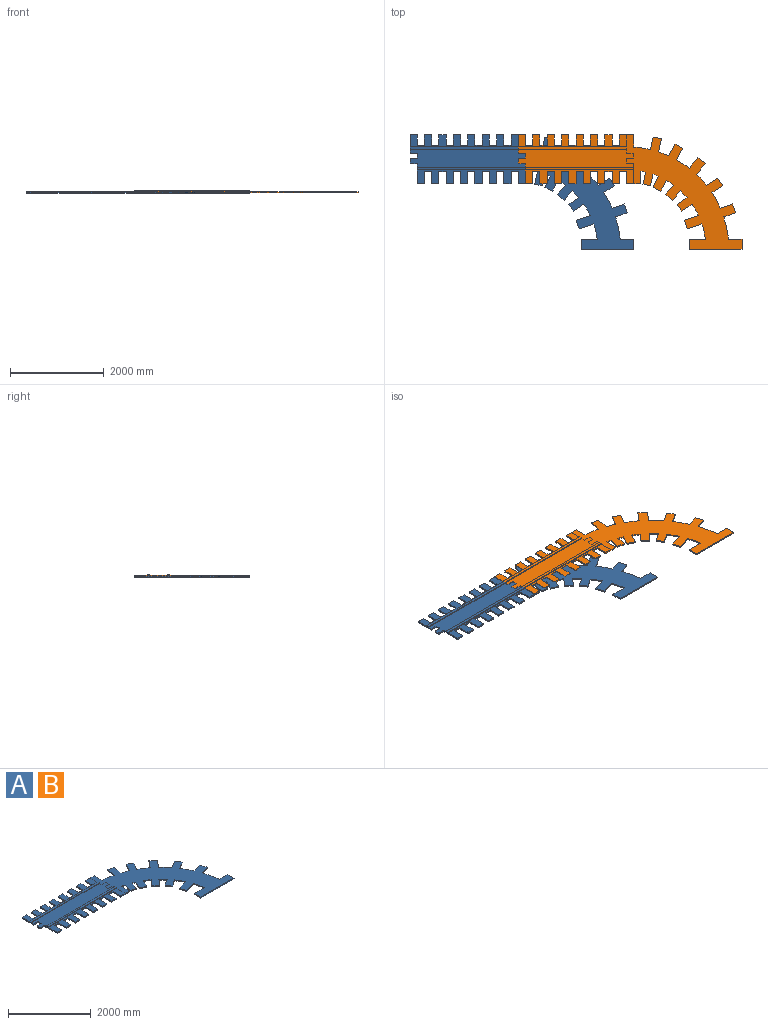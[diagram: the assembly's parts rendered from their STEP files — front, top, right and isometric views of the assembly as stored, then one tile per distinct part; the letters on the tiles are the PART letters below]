
ASSEMBLY  parts=2 mates=1
PART A: 155 faces, bbox 4783.5x2449.5x50.8 mm
  f0: plane 427.85x31.75mm, normal (1,0,0), area 2730.3mm2, adj f4,f67,f68,f86,f97,f137
  f1: plane 294.58x31.75mm, normal (-1,0,0), area 9353.1mm2, adj f4,f39,f86,f95
  f2: plane 81.11x31.75mm, normal (-1,0,0), area 2575.3mm2, adj f4,f29,f86,f88
  f3: plane 81.11x31.75mm, normal (1,0,0), area 2575.3mm2, adj f4,f76,f86,f88,f98
  f4: plane 2468.9x728.98mm, normal (0,0,1), area 1276293.4mm2, adj f0,f1,f2,f3,f29,f30,f31,f32
  f5: plane 154.31x31.75mm, normal (0,1,0), area 4899.2mm2, adj f6,f84,f85,f86
  f6: plane 228.83x31.75mm, normal (1,0,0), area 7265.3mm2, adj f5,f7,f85,f86
  f7: plane 154.31x31.75mm, normal (0,1,0), area 4899.2mm2, adj f6,f8,f85,f86
  f8: plane 228.83x31.75mm, normal (-1,0,0), area 7265.3mm2, adj f7,f9,f85,f86
  f9: plane 154.31x31.75mm, normal (0,1,0), area 4899.2mm2, adj f8,f10,f85,f86
  f10: plane 228.83x31.75mm, normal (1,0,0), area 7265.3mm2, adj f9,f11,f85,f86
  f11: plane 154.31x31.75mm, normal (0,1,0), area 4899.2mm2, adj f10,f12,f85,f86
  f12: plane 228.83x31.75mm, normal (-1,0,0), area 7265.3mm2, adj f11,f13,f85,f86
  f13: plane 154.31x31.75mm, normal (0,1,0), area 4899.2mm2, adj f12,f14,f85,f86
  f14: plane 228.83x31.75mm, normal (1,0,0), area 7265.3mm2, adj f13,f15,f85,f86
  f15: plane 154.31x31.75mm, normal (0,1,0), area 4899.2mm2, adj f14,f16,f85,f86
  f16: plane 228.83x31.75mm, normal (-1,0,0), area 7265.3mm2, adj f15,f17,f85,f86
  f17: plane 154.31x31.75mm, normal (0,1,0), area 4899.2mm2, adj f16,f18,f85,f86
  f18: plane 227.75x31.75mm, normal (1,0,0), area 7231mm2, adj f17,f19,f85,f86
  f19: plane 154.31x31.75mm, normal (0,1,0), area 4899.2mm2, adj f18,f20,f85,f86
  f20: plane 227.75x31.75mm, normal (-1,0,0), area 7231mm2, adj f19,f21,f85,f86
  f21: plane 154.31x31.75mm, normal (0,1,0), area 4899.2mm2, adj f20,f22,f85,f86
  f22: plane 227.75x31.75mm, normal (1,0,0), area 7231mm2, adj f21,f23,f85,f86
  f23: plane 154.31x31.75mm, normal (0,1,0), area 4899.2mm2, adj f22,f24,f85,f86
  f24: plane 227.75x31.75mm, normal (-1,0,0), area 7231mm2, adj f23,f25,f85,f86
  f25: plane 154.31x31.75mm, normal (0,1,0), area 4899.2mm2, adj f24,f26,f85,f86
  f26: plane 227.75x31.75mm, normal (1,0,0), area 7231mm2, adj f25,f27,f85,f86
  f27: plane 154.31x31.75mm, normal (0,1,0), area 4899.2mm2, adj f26,f28,f85,f86
  f28: plane 261.62x31.75mm, normal (-1,0,0), area 8306.5mm2, adj f27,f85,f86,f90
  f29: plane 141.61x31.75mm, normal (0,-1,0), area 4496mm2, adj f2,f4,f30,f86
  f30: cylinder r=12.7mm len=31.75mm, axis (0,0,-1), area 633.4mm2, adj f4,f29,f31,f86
  f31: plane 84.61x31.75mm, normal (-1,0,0), area 2686.3mm2, adj f4,f30,f32,f86
  f32: cylinder r=12.7mm len=31.75mm, axis (0,0,-1), area 633.4mm2, adj f4,f31,f33,f86
  f33: plane 128.91x31.75mm, normal (0,1,0), area 4092.7mm2, adj f4,f32,f34,f86
  f34: cylinder r=12.7mm len=31.75mm, axis (0,0,-1), area 633.4mm2, adj f4,f33,f35,f86
  f35: plane 84.61x31.75mm, normal (-1,0,0), area 2686.3mm2, adj f4,f34,f36,f86
  f36: cylinder r=12.7mm len=31.75mm, axis (0,0,-1), area 633.4mm2, adj f4,f35,f37,f86
  f37: plane 141.61x31.75mm, normal (0,-1,0), area 4496mm2, adj f4,f36,f38,f86
  f38: plane 76.12x31.75mm, normal (-1,0,0), area 2416.8mm2, adj f4,f37,f86,f93
  f39: plane 154.31x31.75mm, normal (0,-1,0), area 4899.5mm2, adj f1,f4,f40,f86
  f40: plane 258.05x31.75mm, normal (1,0,0), area 8193.2mm2, adj f4,f39,f41,f86
  f41: plane 154.31x31.75mm, normal (0,-1,0), area 4899.2mm2, adj f4,f40,f42,f86
  f42: plane 258.05x31.75mm, normal (-1,0,0), area 8193.2mm2, adj f4,f41,f43,f86
  f43: plane 154.31x31.75mm, normal (0,-1,0), area 4899.5mm2, adj f4,f42,f44,f86
  f44: plane 258.05x31.75mm, normal (1,0,0), area 8193.2mm2, adj f4,f43,f45,f86
  f45: plane 154.31x31.75mm, normal (0,-1,0), area 4899.2mm2, adj f4,f44,f46,f86
  f46: plane 258.05x31.75mm, normal (-1,0,0), area 8193.2mm2, adj f4,f45,f47,f86
  f47: plane 154.31x31.75mm, normal (0,-1,0), area 4899.2mm2, adj f4,f46,f48,f86
  f48: plane 258.05x31.75mm, normal (1,0,0), area 8193.2mm2, adj f4,f47,f49,f86
  f49: plane 154.31x31.75mm, normal (0,-1,0), area 4899.2mm2, adj f4,f48,f50,f86
  f50: plane 258.05x31.75mm, normal (-1,0,0), area 8193.2mm2, adj f4,f49,f51,f86
  f51: plane 154.31x31.75mm, normal (0,-1,0), area 4899.2mm2, adj f4,f50,f52,f86
  f52: plane 258.05x31.75mm, normal (1,0,0), area 8193.2mm2, adj f4,f51,f53,f86
  f53: plane 154.31x31.75mm, normal (0,-1,0), area 4899.2mm2, adj f4,f52,f54,f86
  f54: plane 258.05x31.75mm, normal (-1,0,0), area 8193.2mm2, adj f4,f53,f55,f86
  f55: plane 154.31x31.75mm, normal (0,-1,0), area 4899.2mm2, adj f4,f54,f56,f86
  f56: plane 258.05x31.75mm, normal (1,0,0), area 8193.2mm2, adj f4,f55,f57,f86
  f57: plane 154.31x31.75mm, normal (0,-1,0), area 4899.2mm2, adj f4,f56,f58,f86
  f58: plane 258.05x31.75mm, normal (-1,0,0), area 8193.2mm2, adj f4,f57,f59,f86
  f59: plane 154.31x31.75mm, normal (0,-1,0), area 4899.2mm2, adj f4,f58,f60,f86
  f60: plane 258.05x31.75mm, normal (1,0,0), area 8193.2mm2, adj f4,f59,f61,f86
  f61: plane 154.31x31.75mm, normal (0,-1,0), area 4899.2mm2, adj f4,f60,f62,f86
  f62: plane 258.05x31.75mm, normal (-1,0,0), area 8193.2mm2, adj f4,f61,f63,f86
  f63: plane 154.31x31.75mm, normal (0,-1,0), area 4899.2mm2, adj f4,f62,f64,f86
  f64: plane 258.05x31.75mm, normal (1,0,0), area 8193.2mm2, adj f4,f63,f65,f86
  f65: plane 154.31x31.75mm, normal (0,-1,0), area 4899.2mm2, adj f4,f64,f66,f86
  f66: plane 258.05x31.75mm, normal (-1,0,0), area 8193.2mm2, adj f4,f65,f67,f86
  f67: plane 154.31x31.75mm, normal (0,-1,0), area 4899.2mm2, adj f0,f4,f66,f86
  f68: plane 141.61x6.35mm, normal (0,1,0), area 899.2mm2, adj f0,f4,f69,f97
  f69: cylinder r=12.7mm len=12.7mm, axis (0,0,-1), area 126.7mm2, adj f4,f68,f70,f97
  f70: plane 84.61x6.35mm, normal (1,0,0), area 537.3mm2, adj f4,f69,f71,f97
  f71: cylinder r=12.7mm len=12.7mm, axis (0,0,-1), area 126.7mm2, adj f4,f70,f72,f97
  f72: plane 128.91x6.35mm, normal (0,-1,0), area 818.5mm2, adj f4,f71,f73,f97
  f73: cylinder r=12.7mm len=31.75mm, axis (0,0,-1), area 325.9mm2, adj f4,f72,f74,f86,f97,f100
  f74: plane 84.61x31.75mm, normal (1,0,0), area 2686.3mm2, adj f4,f73,f75,f86
  f75: cylinder r=12.7mm len=31.75mm, axis (0,0,-1), area 633.4mm2, adj f4,f74,f76,f86,f99
  f76: plane 141.61x6.35mm, normal (0,1,0), area 899.2mm2, adj f3,f4,f75,f97
  f77: plane 33.88x31.75mm, normal (1,0,0), area 1075.5mm2, adj f78,f85,f86,f90
  f78: plane 228.83x31.75mm, normal (1,0,0), area 7265.3mm2, adj f77,f79,f85,f86
  f79: plane 154.31x31.75mm, normal (0,1,0), area 4899.2mm2, adj f78,f80,f85,f86
  f80: plane 228.83x31.75mm, normal (-1,0,0), area 7265.3mm2, adj f79,f81,f85,f86
  f81: plane 154.31x31.75mm, normal (0,1,0), area 4899.2mm2, adj f80,f82,f85,f86
  f82: plane 228.83x31.75mm, normal (1,0,0), area 7265.3mm2, adj f81,f83,f85,f86
  f83: plane 154.31x31.75mm, normal (0,1,0), area 4899.2mm2, adj f82,f84,f85,f86
  f84: plane 228.83x31.75mm, normal (-1,0,0), area 7265.3mm2, adj f5,f83,f85,f86
  f85: plane 2314.58x262.7mm, normal (0,0,1), area 360381.5mm2, adj f5,f6,f7,f8,f9,f10,f11,f12
  f86: plane 4783.48x2449.54mm, normal (0,0,-1), area 4101980.7mm2, adj f0,f1,f2,f3,f5,f6,f7,f8
  f87: plane 57.15x50.8mm, normal (-1,0,0), area 2903.2mm2, adj f86,f88,f90,f91
  f88: plane 2314.86x50.8mm, normal (0,-1,0), area 44106.9mm2, adj f2,f3,f4,f86,f87,f89,f91,f98
  f89: plane 57.15x25.4mm, normal (1,0,0), area 1451.6mm2, adj f88,f90,f91,f97
  f90: plane 2314.86x50.8mm, normal (0,1,0), area 44107.1mm2, adj f28,f77,f85,f86,f87,f89,f91,f134
  f91: plane 2314.86x57.15mm, normal (0,0,1), area 132294.4mm2, adj f87,f88,f89,f90
  f92: plane 57.15x19.05mm, normal (1,0,0), area 1088.7mm2, adj f4,f93,f95,f96
  f93: plane 2314.7x50.8mm, normal (0,1,0), area 44104.6mm2, adj f4,f38,f86,f92,f94,f96
  f94: plane 57.15x50.8mm, normal (-1,0,0), area 2903.2mm2, adj f86,f93,f95,f96
  f95: plane 2314.7x50.8mm, normal (0,-1,0), area 44104.6mm2, adj f1,f4,f86,f92,f94,f96
  f96: plane 2314.7x57.15mm, normal (0,0,1), area 132285.3mm2, adj f92,f93,f94,f95
  f97: plane 2468.62x2449.52mm, normal (0,0,1), area 2200726.2mm2, adj f0,f68,f69,f70,f71,f72,f73,f76
  f98: plane 81.11x25.4mm, normal (-1,0,0), area 2060.2mm2, adj f3,f86,f88,f97
  f99: plane 25.4x0.66mm, normal (0,-1,0), area 16.8mm2, adj f75,f86,f97,f135
  f100: cylinder r=12.7mm len=25.4mm, axis (0,0,-1), area 226.5mm2, adj f73,f86,f97,f136
  f101: cylinder r=1700.76mm len=237.49mm, axis (0,0,-1), area 6962.1mm2, adj f86,f97,f102,f154
  f102: plane 302.61x103.69mm, normal (-0.32,0.95,0), area 8125mm2, adj f86,f97,f101,f103
  f103: plane 186.47x63.9mm, normal (-0.95,-0.32,0), area 5006.7mm2, adj f86,f97,f102,f104
  f104: plane 312.34x107.03mm, normal (0.32,-0.95,0), area 8386.3mm2, adj f86,f97,f103,f105
  f105: cylinder r=1700.76mm len=325.23mm, axis (0,0,-1), area 8489.9mm2, adj f86,f97,f104,f106
  f106: plane 344.05x25.4mm, normal (0,1,0), area 8738.8mm2, adj f86,f97,f105,f107
  f107: plane 216.55x25.4mm, normal (-1,0,0), area 5500.4mm2, adj f86,f97,f106,f108
  f108: plane 1125.75x25.4mm, normal (0,-1,0), area 28594mm2, adj f86,f97,f107,f109
  f109: plane 216.55x25.4mm, normal (1,0,0), area 5500.4mm2, adj f86,f97,f108,f110
  f110: plane 289.07x25.4mm, normal (0,1,0), area 7342.3mm2, adj f86,f97,f109,f111
  f111: cylinder r=2190.28mm len=476.04mm, axis (0,0,-1), area 12389.7mm2, adj f86,f97,f110,f112
  f112: plane 253.14x88.05mm, normal (0.33,-0.94,0), area 6807.7mm2, adj f86,f97,f111,f113
  f113: plane 188.6x65.6mm, normal (0.94,0.33,0), area 5071.8mm2, adj f86,f97,f112,f114
  f114: plane 259.3x90.19mm, normal (-0.33,0.94,0), area 6973.2mm2, adj f86,f97,f113,f115
  f115: cylinder r=2190.28mm len=331.98mm, axis (0,0,-1), area 9617.4mm2, adj f86,f97,f114,f116
  f116: plane 231.02x148.34mm, normal (0.54,-0.84,0), area 6973.5mm2, adj f86,f97,f115,f117
  f117: plane 158.35x101.68mm, normal (0.84,0.54,0), area 4779.8mm2, adj f86,f97,f116,f118
  f118: plane 240.23x154.25mm, normal (-0.54,0.84,0), area 7251.4mm2, adj f86,f97,f117,f119
  f119: cylinder r=2190.28mm len=237.38mm, axis (0,0,-1), area 8215.6mm2, adj f86,f97,f118,f120
  f120: plane 229.27x190.03mm, normal (0.77,-0.64,0), area 7563.7mm2, adj f86,f97,f119,f121
  f121: plane 157.87x130.85mm, normal (0.64,0.77,0), area 5208.2mm2, adj f86,f97,f120,f122
  f122: plane 227.33x188.43mm, normal (-0.77,0.64,0), area 7499.9mm2, adj f86,f97,f121,f123
  f123: cylinder r=2190.28mm len=271.55mm, axis (0,0,-1), area 8270.9mm2, adj f86,f97,f122,f124
  f124: plane 246.94x132.44mm, normal (0.88,-0.47,0), area 7117.5mm2, adj f86,f97,f123,f125
  f125: plane 164.65x88.3mm, normal (0.47,0.88,0), area 4745.7mm2, adj f86,f97,f124,f126
  f126: plane 251.24x134.74mm, normal (-0.88,0.47,0), area 7241.3mm2, adj f86,f97,f125,f127
  f127: cylinder r=2190.28mm len=215.38mm, axis (0,0,-1), area 5872.2mm2, adj f86,f97,f126,f128
  f128: plane 278.99x62.62mm, normal (0.98,-0.22,0), area 7262.7mm2, adj f86,f97,f127,f129
  f129: plane 178.6x40.08mm, normal (0.22,0.98,0), area 4649.4mm2, adj f86,f97,f128,f130
  f130: plane 269.11x60.4mm, normal (-0.98,0.22,0), area 7005.3mm2, adj f86,f97,f129,f131
  f131: cylinder r=2190.28mm len=356.31mm, axis (0,0,-1), area 9166mm2, adj f86,f97,f130,f132
  f132: plane 264.52x25.4mm, normal (1,0,0), area 6718.9mm2, adj f86,f97,f131,f133
  f133: plane 152.02x25.4mm, normal (0,1,0), area 3861.3mm2, adj f86,f97,f132,f134
  f134: plane 262.69x25.4mm, normal (-1,0,0), area 6672.2mm2, adj f86,f90,f97,f133
  f135: cylinder r=12.7mm len=25.4mm, axis (0,0,-1), area 506.7mm2, adj f86,f97,f99,f136
  f136: plane 83.76x25.4mm, normal (-1,0,0), area 2127.5mm2, adj f86,f97,f100,f135
  f137: plane 149.34x25.4mm, normal (0,-1,0), area 3793.2mm2, adj f0,f86,f97,f138
  f138: plane 272.2x25.4mm, normal (1,0,0), area 6913.9mm2, adj f86,f97,f137,f139
  f139: cylinder r=1700.76mm len=102.87mm, axis (0,0,-1), area 2672.2mm2, adj f86,f97,f138,f140
  f140: plane 258.4x55.67mm, normal (-0.98,0.21,0), area 6714mm2, adj f86,f97,f139,f141
  f141: plane 160.58x34.6mm, normal (-0.21,-0.98,0), area 4172.3mm2, adj f86,f97,f140,f142
  f142: plane 245.91x52.98mm, normal (0.98,-0.21,0), area 6389.5mm2, adj f86,f97,f141,f143
  f143: cylinder r=1700.76mm len=114.49mm, axis (0,0,-1), area 3125.1mm2, adj f86,f97,f142,f144
  f144: plane 236.07x112.34mm, normal (-0.9,0.43,0), area 6640.5mm2, adj f86,f97,f143,f145
  f145: plane 169.2x80.52mm, normal (-0.43,-0.9,0), area 4759.6mm2, adj f86,f97,f144,f146
  f146: plane 232.42x110.6mm, normal (0.9,-0.43,0), area 6537.8mm2, adj f86,f97,f145,f147
  f147: cylinder r=1700.76mm len=163.29mm, axis (0,0,-1), area 4955.3mm2, adj f86,f97,f146,f148
  f148: plane 191.84x169.32mm, normal (-0.75,0.66,0), area 6499.1mm2, adj f86,f97,f147,f149
  f149: plane 141.48x124.87mm, normal (-0.66,-0.75,0), area 4793.2mm2, adj f86,f97,f148,f150
  f150: plane 196.37x173.31mm, normal (0.75,-0.66,0), area 6652.6mm2, adj f86,f97,f149,f151
  f151: cylinder r=1700.76mm len=144.46mm, axis (0,0,-1), area 5090.4mm2, adj f86,f97,f150,f152
  f152: plane 212.37x140.17mm, normal (-0.55,0.83,0), area 6463.2mm2, adj f86,f97,f151,f153
  f153: plane 148.36x97.92mm, normal (-0.83,-0.55,0), area 4515.2mm2, adj f86,f97,f152,f154
  f154: plane 222.85x147.09mm, normal (0.55,-0.83,0), area 6782.1mm2, adj f86,f97,f101,f153
PART B: same geometry as A
PLACE A t=(153.58,127.5,770.51)mm
PLACE B t=(2468.17,127.5,783.21)mm
MATE fastened B.f35 <-> A.f70  axis (-1,0,0) through (153.58,-37.51,799.09)mm
